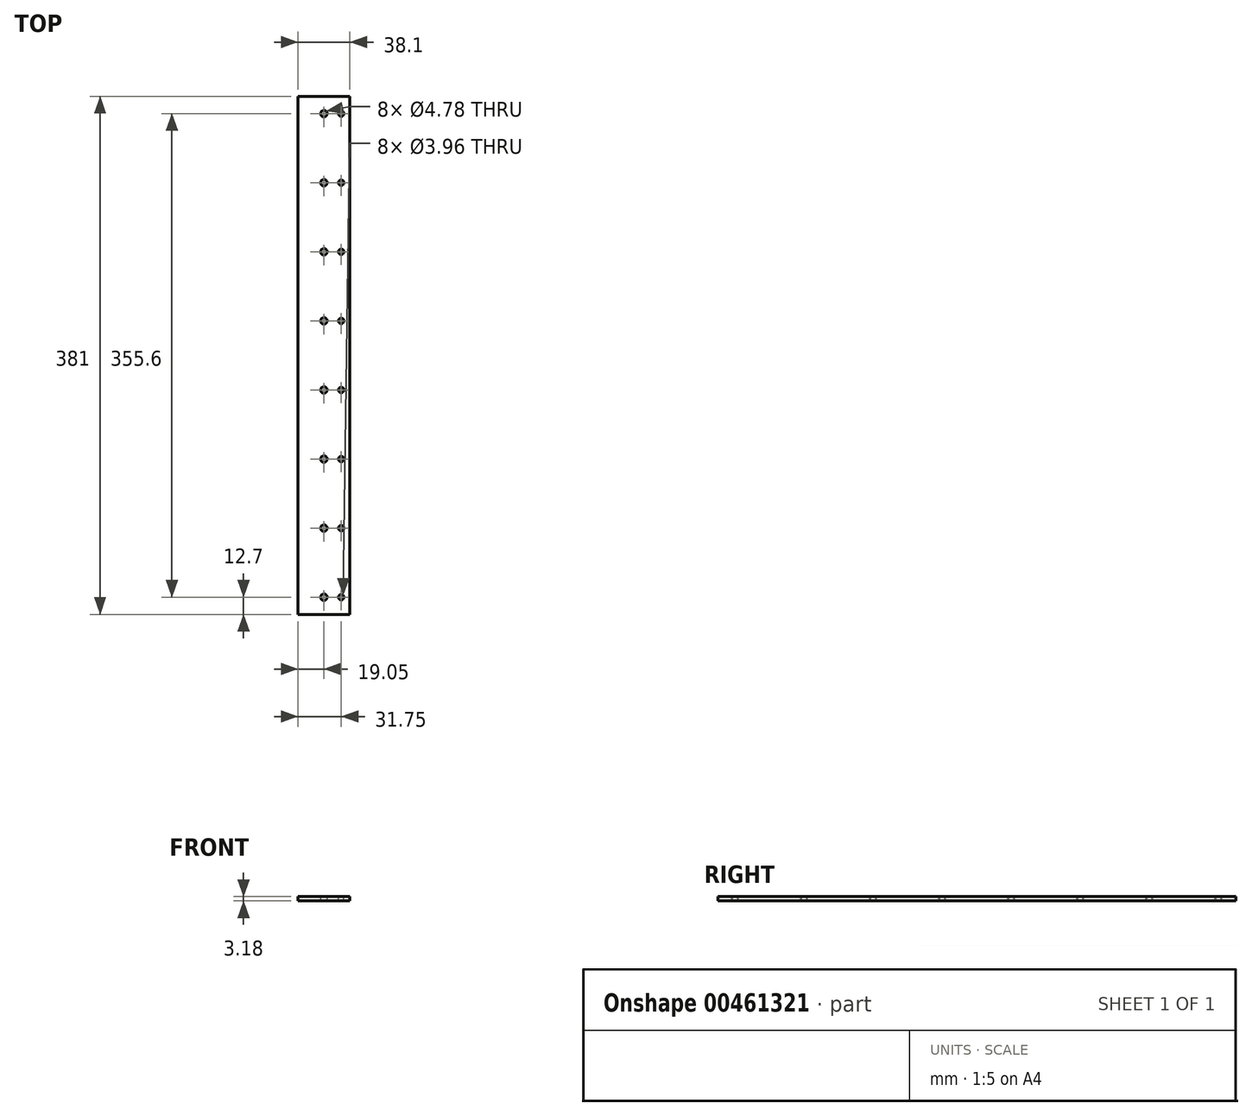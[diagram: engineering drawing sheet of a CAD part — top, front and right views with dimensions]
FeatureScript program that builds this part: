
annotation { "Feature Type Name" : "Feature", "Feature Type Description" : "" }
export const myFeature = defineFeature(function(context is Context, id is Id, definition is map)
    precondition{}
    {
        {
            var Q0;
            Q0=qCreatedBy(makeId("Front.planeOp"),FACE);
            var sketch = newSketch(context, id + "F0", { "sketchPlane" : qUnion([Q0])});
            skLineSegment(sketch, "E0.bottom", {"start": v(0, 0) * mm, "end": v(38.1, 0) * mm});
            skLineSegment(sketch, "E0.top", {"start": v(0, 3.17) * mm, "end": v(38.1, 3.17) * mm});
            skLineSegment(sketch, "E0.left", {"start": v(0, 0) * mm, "end": v(0, 3.17) * mm});
            skLineSegment(sketch, "E0.right", {"start": v(38.1, 0) * mm, "end": v(38.1, 3.17) * mm});
            skSolve(sketch);
        }
        {
            var Q0;
            Q0=makeQuery(id+"F0.imprint","IMPRINT",FACE,{"disambiguationData":[TD([[makeQuery(id+"F0.imprint","IMPRINT",EDGE,{"derivedFrom":sQuery(id+"F0.wireOp",EDGE,"E0.bottom")}),1.0]])]});
            extrude(context, id + "F1", {"entities" : qUnion([Q0]), "depth" : 381 * mm});
        }
        {
            var Q0;
            Q0=makeQuery(id+"F1.opExtrude","SWEPT_FACE",FACE,{"disambiguationData":[OSD([sQuery(id+"F0.wireOp",EDGE,"E0.top")])]});
            var sketch = newSketch(context, id + "F2", { "sketchPlane" : qUnion([Q0])});
            skCircle(sketch, "E1", {"center": v(19.05, -12.7) * mm, "radius": 2.39 * mm});
            skCircle(sketch, "E2", {"center": v(31.75, -12.7) * mm, "radius": 1.98 * mm});
            skCircle(sketch, "E3.0.1.0", {"center": v(19.05, -63.5) * mm, "radius": 2.39 * mm});
            skCircle(sketch, "E3.0.1.1", {"center": v(31.75, -63.5) * mm, "radius": 1.98 * mm});
            skCircle(sketch, "E3.0.2.0", {"center": v(19.05, -114.3) * mm, "radius": 2.39 * mm});
            skCircle(sketch, "E3.0.2.1", {"center": v(31.75, -114.3) * mm, "radius": 1.98 * mm});
            skCircle(sketch, "E3.0.3.0", {"center": v(19.05, -165.1) * mm, "radius": 2.39 * mm});
            skCircle(sketch, "E3.0.3.1", {"center": v(31.75, -165.1) * mm, "radius": 1.98 * mm});
            skCircle(sketch, "E3.0.4.0", {"center": v(19.05, -215.9) * mm, "radius": 2.39 * mm});
            skCircle(sketch, "E3.0.4.1", {"center": v(31.75, -215.9) * mm, "radius": 1.98 * mm});
            skCircle(sketch, "E3.0.5.0", {"center": v(19.05, -266.7) * mm, "radius": 2.39 * mm});
            skCircle(sketch, "E3.0.5.1", {"center": v(31.75, -266.7) * mm, "radius": 1.98 * mm});
            skCircle(sketch, "E3.0.6.0", {"center": v(19.05, -317.5) * mm, "radius": 2.39 * mm});
            skCircle(sketch, "E3.0.6.1", {"center": v(31.75, -317.5) * mm, "radius": 1.98 * mm});
            skCircle(sketch, "E3.0.7.0", {"center": v(19.05, -368.3) * mm, "radius": 2.39 * mm});
            skCircle(sketch, "E3.0.7.1", {"center": v(31.75, -368.3) * mm, "radius": 1.98 * mm});
            skLineSegment(sketch, "E3.direction1", {"start": v(19.05, -12.7) * mm, "end": v(44.45, -12.7) * mm, "construction": true});
            skLineSegment(sketch, "E3.direction2", {"start": v(19.05, -12.7) * mm, "end": v(19.05, -63.5) * mm, "construction": true});
            skSolve(sketch);
        }
        {
            var Q0;
            Q0=makeQuery(id+"F2.imprint","IMPRINT",FACE,{"disambiguationData":[TD([[makeQuery(id+"F2.imprint","IMPRINT",EDGE,{"derivedFrom":sQuery(id+"F2.wireOp",EDGE,"E3.0.7.0")}),1.0]])]});
            var Q1;
            Q1=makeQuery(id+"F2.imprint","IMPRINT",FACE,{"disambiguationData":[TD([[makeQuery(id+"F2.imprint","IMPRINT",EDGE,{"derivedFrom":sQuery(id+"F2.wireOp",EDGE,"E3.0.7.1")}),1.0]])]});
            var Q2;
            Q2=makeQuery(id+"F2.imprint","IMPRINT",FACE,{"disambiguationData":[TD([[makeQuery(id+"F2.imprint","IMPRINT",EDGE,{"derivedFrom":sQuery(id+"F2.wireOp",EDGE,"E3.0.6.0")}),1.0]])]});
            var Q3;
            Q3=makeQuery(id+"F2.imprint","IMPRINT",FACE,{"disambiguationData":[TD([[makeQuery(id+"F2.imprint","IMPRINT",EDGE,{"derivedFrom":sQuery(id+"F2.wireOp",EDGE,"E3.0.6.1")}),1.0]])]});
            var Q4;
            Q4=makeQuery(id+"F2.imprint","IMPRINT",FACE,{"disambiguationData":[TD([[makeQuery(id+"F2.imprint","IMPRINT",EDGE,{"derivedFrom":sQuery(id+"F2.wireOp",EDGE,"E3.0.5.0")}),1.0]])]});
            var Q5;
            Q5=makeQuery(id+"F2.imprint","IMPRINT",FACE,{"disambiguationData":[TD([[makeQuery(id+"F2.imprint","IMPRINT",EDGE,{"derivedFrom":sQuery(id+"F2.wireOp",EDGE,"E3.0.5.1")}),1.0]])]});
            var Q6;
            Q6=makeQuery(id+"F2.imprint","IMPRINT",FACE,{"disambiguationData":[TD([[makeQuery(id+"F2.imprint","IMPRINT",EDGE,{"derivedFrom":sQuery(id+"F2.wireOp",EDGE,"E3.0.4.0")}),1.0]])]});
            var Q7;
            Q7=makeQuery(id+"F2.imprint","IMPRINT",FACE,{"disambiguationData":[TD([[makeQuery(id+"F2.imprint","IMPRINT",EDGE,{"derivedFrom":sQuery(id+"F2.wireOp",EDGE,"E3.0.4.1")}),1.0]])]});
            var Q8;
            Q8=makeQuery(id+"F2.imprint","IMPRINT",FACE,{"disambiguationData":[TD([[makeQuery(id+"F2.imprint","IMPRINT",EDGE,{"derivedFrom":sQuery(id+"F2.wireOp",EDGE,"E3.0.3.1")}),1.0]])]});
            var Q9;
            Q9=makeQuery(id+"F2.imprint","IMPRINT",FACE,{"disambiguationData":[TD([[makeQuery(id+"F2.imprint","IMPRINT",EDGE,{"derivedFrom":sQuery(id+"F2.wireOp",EDGE,"E3.0.3.0")}),1.0]])]});
            var Q10;
            Q10=makeQuery(id+"F2.imprint","IMPRINT",FACE,{"disambiguationData":[TD([[makeQuery(id+"F2.imprint","IMPRINT",EDGE,{"derivedFrom":sQuery(id+"F2.wireOp",EDGE,"E3.0.2.0")}),1.0]])]});
            var Q11;
            Q11=makeQuery(id+"F2.imprint","IMPRINT",FACE,{"disambiguationData":[TD([[makeQuery(id+"F2.imprint","IMPRINT",EDGE,{"derivedFrom":sQuery(id+"F2.wireOp",EDGE,"E3.0.2.1")}),1.0]])]});
            var Q12;
            Q12=makeQuery(id+"F2.imprint","IMPRINT",FACE,{"disambiguationData":[TD([[makeQuery(id+"F2.imprint","IMPRINT",EDGE,{"derivedFrom":sQuery(id+"F2.wireOp",EDGE,"E3.0.1.0")}),1.0]])]});
            var Q13;
            Q13=makeQuery(id+"F2.imprint","IMPRINT",FACE,{"disambiguationData":[TD([[makeQuery(id+"F2.imprint","IMPRINT",EDGE,{"derivedFrom":sQuery(id+"F2.wireOp",EDGE,"E3.0.1.1")}),1.0]])]});
            var Q14;
            Q14=makeQuery(id+"F2.imprint","IMPRINT",FACE,{"disambiguationData":[TD([[makeQuery(id+"F2.imprint","IMPRINT",EDGE,{"derivedFrom":sQuery(id+"F2.wireOp",EDGE,"E1")}),1.0]])]});
            var Q15;
            Q15=makeQuery(id+"F2.imprint","IMPRINT",FACE,{"disambiguationData":[TD([[makeQuery(id+"F2.imprint","IMPRINT",EDGE,{"derivedFrom":sQuery(id+"F2.wireOp",EDGE,"E2")}),1.0]])]});
            extrude(context, id + "F3", {"entities" : qUnion([Q0, Q1, Q2, Q3, Q4, Q5, Q6, Q7, Q8, Q9, Q10, Q11, Q12, Q13, Q14, Q15]), "operationType" : NewBodyOperationType.REMOVE, "oppositeDirection" : true, "depth" : 25.4 * mm});
        }
    });
